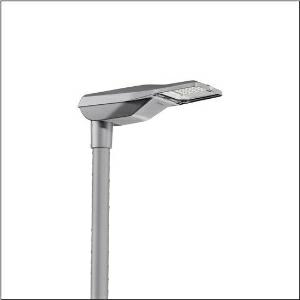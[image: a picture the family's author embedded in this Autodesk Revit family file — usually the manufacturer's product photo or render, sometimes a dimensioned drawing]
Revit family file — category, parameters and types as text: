
# Revit family: streetlight_sl_21_iq_micro___st1_0a_5xe1d61g08cb_d415
name_source: partatom
category: Lighting Fixtures
units: mm (PartAtom-declared; Revit-internal decimal feet)

## family parameters
Cut with Voids When Loaded = No
Host = Face
Light Source = No
Part Type = Normal
Room Calculation Point = No
Round Connector Dimension = Use Diameter
Shared = No

## types (1)
- --- (1 x LED, 2570 lm, 19.4 W, 2700K)
    Apparent Load = 19 VA
    CIE Flux Codes = 37 72 97 100 100
    Color Rendering = 70
    Color Temperature = 2700K
    Default Elevation = 1800 mm
    Description = Streetlight SL 21 iQ micro, mast luminaire, primary light control with lens, of PMMA, primary optical cover: cover, of toughened safety glass, transparent, light distribution: ST1.0a, light emission: direct distribution, primary light characteristic: asymmetric, installation type: post-top, side-entry, LED, High Power LED, rated luminous flux: 2.570lm, luminous efficacy: 133lm/W, light colour: 727, colour temperature: 2700K, control gear: iQ Street-Remote, control: Street-Remote, Auto-Match, Temp-Guard, Lumen-Switch, Night-Set, Smart-Wire, Light-Fading, Desk-Remote (wireless, voltage-free reading and setting of iQ features in the workshop via application-optimized NFC function/RFID function), optimised constant luminous flux control (CLO 2.0), pre-setting: linear dimming characteristic, mains connection: 220..240V, AC, 50/60Hz, start of lifetime: 19W, end of service life: 20W, reduction: 10W, luminaire housing, of diecast aluminium, powder-coated, SITECO metallic grey (DB 702S), corrosivity category C5 high according to DIN EN ISO 12944, please order mast flange separately, inclination adjustable: 0°, 5°, 10°, 15°, sealing non-destructively replaceable, multi-level sealing system, length: 528mm, width: 235mm, height: 110mm, mast flange for spigot size: 42mm (side-entry): 5XC10008XM4, 60/48mm (side-entry/post-top): 5XC10108XM2, 76/60mm (side-entry/post-top): 5XC10108XM1, protection rating (complete): IP66, insulation class (complete): insulation class II (safety insulation), certification: CE, ENEC, ENEC+, VDE, impact resistance: IK10, permissible operating ambient temperature for outdoor applications: -40..+50°C, standard-compliant lighting for roads and squares, packaging unit: 1 piece

Light Distribution: ST1.0a
    Height = 110 mm
    Lamp = 1 x LED
    Lamp Light Flux = 2570 lm
    Lamp Power = 19.4 W
    Lamp count = 1
    Length = 528 mm
    Luminous efficacy = 132 lm/W
    Manufacturer = Siteco
    ModVariant = No
    Model = 5XE1D61G08CB
    Number of Poles = 1
    OnlyDefault = Yes
    Power Factor = 1
    Product Name = Streetlight SL 21 iQ micro | ST1.0a
    Product group = mast luminaire | pylon top
    ProductGroupID = 6100
    Protection Class = Protection class II
    Protection Degree = IP 66
    RLX_Detail_Level = 1
    RLX_Emergency_Light_Flux = 0 lm
    RLX_Emergency_Type = 0
    RLX_Emergency_Type_DB = No
    RlxData = <blob elided: 99049 chars, md5=b0f3f453>
    Socket = socket
    Standby Power = 0 W
    System Light Flux = 2570 lm
    System Power = 19 W
    Type Comments = factory setting: luminous flux: 100 % | dim-lin: 254 | 387 mA
    Type Image = l_1006881.jpg
    URL = http://relux.com
    VarID = @adj_138603
    Voltage = 0 V
    Weight = 0.00 kg
    Width = 235 mm

## geometry (parser evidence)
native form markers: Blend x4, Sweep x10
no freeform markers — native parametric forms only
